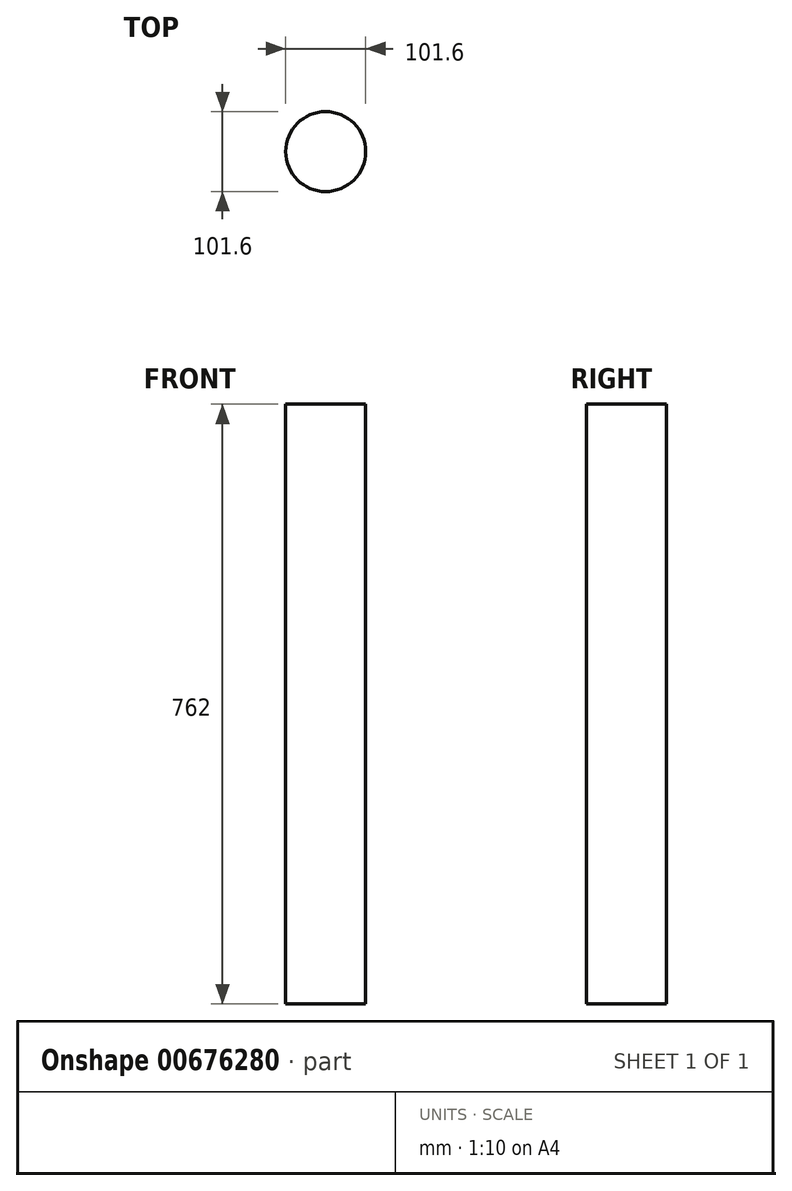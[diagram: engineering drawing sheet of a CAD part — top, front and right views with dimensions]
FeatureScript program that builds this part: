
annotation { "Feature Type Name" : "Feature", "Feature Type Description" : "" }
export const myFeature = defineFeature(function(context is Context, id is Id, definition is map)
    precondition{}
    {
        {
            var Q0;
            Q0=qCreatedBy(makeId("Top.planeOp"),FACE);
            var sketch = newSketch(context, id + "F0", { "sketchPlane" : qUnion([Q0])});
            skCircle(sketch, "E0", {"center": v(0, 0) * mm, "radius": 50.8 * mm});
            skSolve(sketch);
        }
        {
            var Q0;
            Q0 = qSketchRegion(id + "F0", true);
            extrude(context, id + "F1", {"entities" : qUnion([Q0]), "depth" : 762 * mm, "offsetDistance" : 25.4 * mm});
        }
    });
